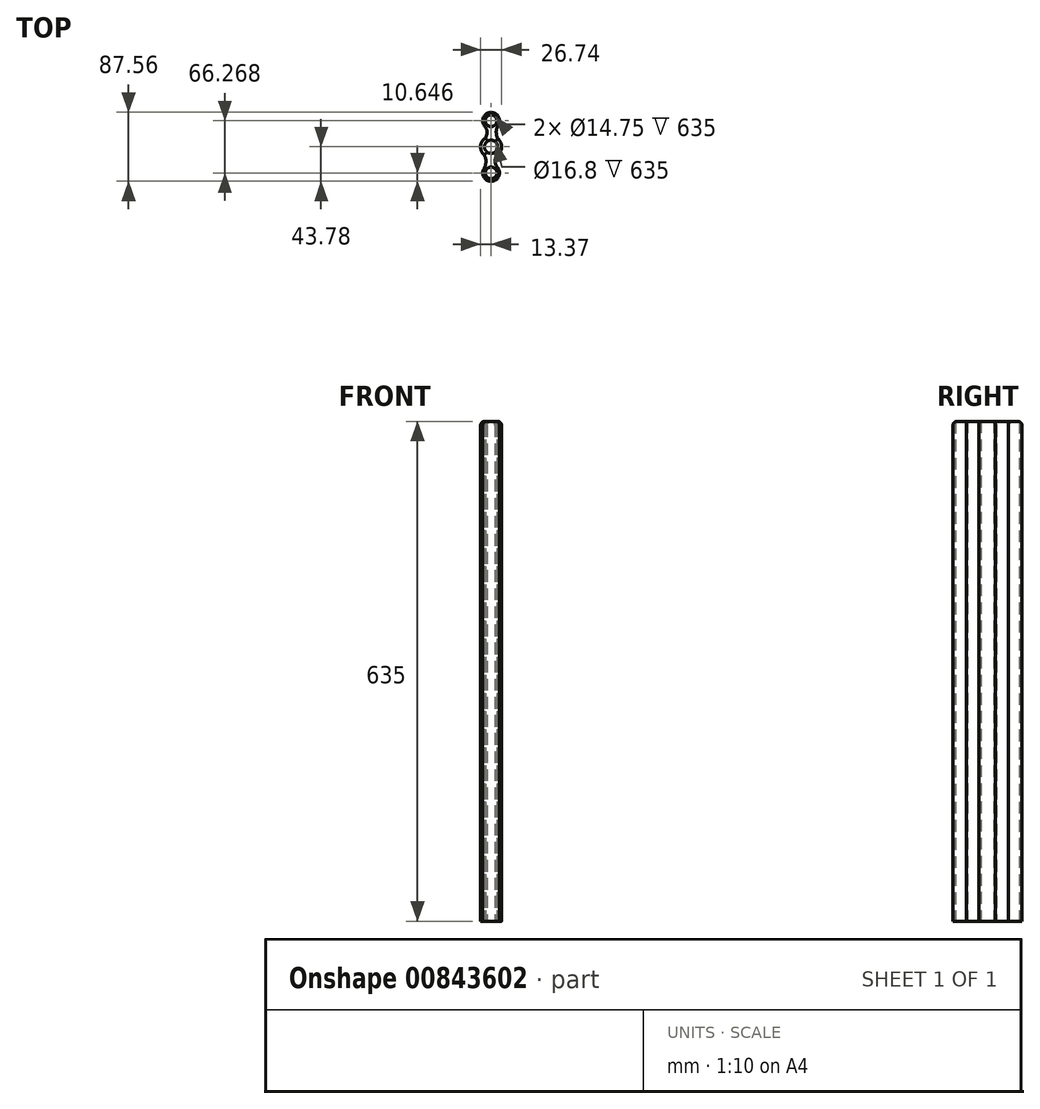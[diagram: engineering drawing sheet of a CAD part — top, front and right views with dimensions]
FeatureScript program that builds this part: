
annotation { "Feature Type Name" : "Feature", "Feature Type Description" : "" }
export const myFeature = defineFeature(function(context is Context, id is Id, definition is map)
    precondition{}
    {
        {
            var Q0;
            Q0=qCreatedBy(makeId("Top.planeOp"),FACE);
            var sketch = newSketch(context, id + "F0", { "sketchPlane" : qUnion([Q0])});
            skCircle(sketch, "E0", {"center": v(0, 0) * mm, "radius": 8.4 * mm});
            skCircle(sketch, "E1", {"center": v(0, 33.13) * mm, "radius": 7.38 * mm});
            skArc(sketch, "E2", {"start": v(8.43, 26.63) * mm, "mid": v(-0.54, 43.77) * mm, "end": v(-7.73, 25.81) * mm});
            skArc(sketch, "E3", {"start": v(-7.34, 11.17) * mm, "mid": v(-13.34, 0.82) * mm, "end": v(-8.65, -10.2) * mm});
            skArc(sketch, "E4", {"start": v(8.43, 26.63) * mm, "mid": v(6.54, 18.39) * mm, "end": v(8.65, 10.2) * mm});
            skArc(sketch, "E5", {"start": v(-7.34, 11.17) * mm, "mid": v(-5.08, 19) * mm, "end": v(-8.31, 26.48) * mm});
            skArc(sketch, "E6.1.0", {"start": v(-8.43, -26.63) * mm, "mid": v(0.54, -43.77) * mm, "end": v(7.73, -25.81) * mm});
            skCircle(sketch, "E6.1.1", {"center": v(0, -33.13) * mm, "radius": 7.38 * mm});
            skArc(sketch, "E6.1.2", {"start": v(7.34, -11.17) * mm, "mid": v(5.08, -19) * mm, "end": v(8.31, -26.48) * mm});
            skArc(sketch, "E6.1.3", {"start": v(-8.43, -26.63) * mm, "mid": v(-6.54, -18.39) * mm, "end": v(-8.65, -10.2) * mm});
            skArc(sketch, "E7.trimOffspring", {"start": v(7.34, -11.17) * mm, "mid": v(13.34, -0.82) * mm, "end": v(8.65, 10.2) * mm});
            skSolve(sketch);
        }
        {
            var Q0;
            Q0=makeQuery(id+"F0.imprint","IMPRINT",FACE,{"disambiguationData":[TD([[makeQuery(id+"F0.imprint","IMPRINT",EDGE,{"derivedFrom":sQuery(id+"F0.wireOp",EDGE,"E0")}),-1.0]])]});
            extrude(context, id + "F1", {"entities" : qUnion([Q0]), "depth" : 635 * mm, "offsetDistance" : 25.4 * mm});
        }
        {
            var Q0;
            Q0=makeQuery(id+"F1.opExtrude","CAP_EDGE",EDGE,{"disambiguationData":[OSD([sQuery(id+"F0.wireOp",EDGE,"E2")])],"isStart":false});
            var Q1;
            Q1=makeQuery(id+"F1.opExtrude","CAP_EDGE",EDGE,{"disambiguationData":[OSD([sQuery(id+"F0.wireOp",EDGE,"E5")])],"isStart":false});
            var Q2;
            Q2=makeQuery(id+"F1.opExtrude","CAP_EDGE",EDGE,{"disambiguationData":[OSD([sQuery(id+"F0.wireOp",EDGE,"E3")])],"isStart":false});
            var Q3;
            Q3=makeQuery(id+"F1.opExtrude","CAP_EDGE",EDGE,{"disambiguationData":[OSD([sQuery(id+"F0.wireOp",EDGE,"E6.1.3")])],"isStart":false});
            var Q4;
            Q4=makeQuery(id+"F1.opExtrude","CAP_EDGE",EDGE,{"disambiguationData":[OSD([sQuery(id+"F0.wireOp",EDGE,"E6.1.0")])],"isStart":false});
            var Q5;
            Q5=makeQuery(id+"F1.opExtrude","CAP_EDGE",EDGE,{"disambiguationData":[OSD([sQuery(id+"F0.wireOp",EDGE,"E6.1.2")])],"isStart":false});
            var Q6;
            Q6=makeQuery(id+"F1.opExtrude","CAP_EDGE",EDGE,{"disambiguationData":[OSD([sQuery(id+"F0.wireOp",EDGE,"E7.trimOffspring")])],"isStart":false});
            var Q7;
            Q7=makeQuery(id+"F1.opExtrude","CAP_EDGE",EDGE,{"disambiguationData":[OSD([sQuery(id+"F0.wireOp",EDGE,"E4")])],"isStart":false});
            fillet(context, id + "F2", {"entities" : qUnion([Q0, Q1, Q2, Q3, Q4, Q5, Q6, Q7]), "radius" : 5.08 * mm, "tangentPropagation" : true, "allowEdgeOverflow" : false});
        }
    });
